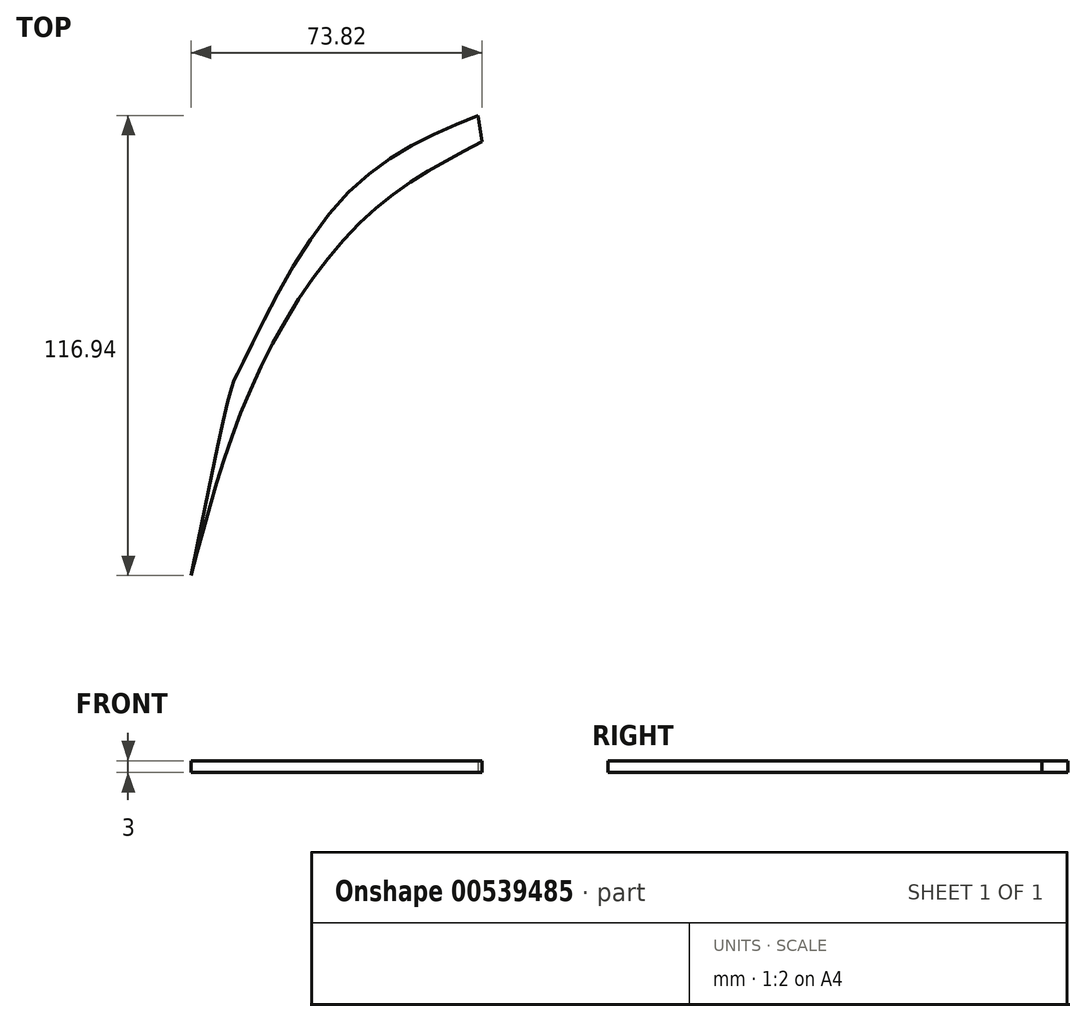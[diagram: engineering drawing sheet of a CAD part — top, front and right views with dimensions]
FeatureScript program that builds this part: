
annotation { "Feature Type Name" : "Feature", "Feature Type Description" : "" }
export const myFeature = defineFeature(function(context is Context, id is Id, definition is map)
    precondition{}
    {
        {
            var Q0;
            Q0=qCreatedBy(makeId("Top.planeOp"),FACE);
            var sketch = newSketch(context, id + "F0", { "sketchPlane" : qUnion([Q0])});
            skLineSegment(sketch, "E0.bottom", {"start": v(-86.95, -34.92) * mm, "end": v(12.45, -34.92) * mm});
            skLineSegment(sketch, "E0.top", {"start": v(-86.95, 85.08) * mm, "end": v(12.45, 85.08) * mm});
            skLineSegment(sketch, "E0.left", {"start": v(-86.95, -34.92) * mm, "end": v(-86.95, 85.08) * mm});
            skLineSegment(sketch, "E0.right", {"start": v(12.45, -34.92) * mm, "end": v(12.45, 85.08) * mm});
            skSolve(sketch);
        }
        {
            var Q0;
            Q0=makeQuery(id+"F0.imprint","IMPRINT",FACE,{"disambiguationData":[TD([[makeQuery(id+"F0.imprint","IMPRINT",EDGE,{"derivedFrom":sQuery(id+"F0.wireOp",EDGE,"E0.bottom")}),1.0]])]});
            var sketch = newSketch(context, id + "F1", { "sketchPlane" : qUnion([Q0])});
            skFitSpline(sketch, "E1", {"points": [v(-82.89, -33.95) * mm, v(-72.6, 14.09) * mm, v(-70.83, 17.96) * mm, v(-46.3, 59.8) * mm, v(-10.03, 82.99) * mm], "startDerivative": vector(41.06, 204.3) * mm, "endDerivative": vector(130.59, 53.62) * mm});
            skFitSpline(sketch, "E2", {"points": [v(-82.89, -33.95) * mm, v(-67.92, 13.16) * mm, v(-39.6, 56.22) * mm, v(-9.07, 76.32) * mm], "startDerivative": vector(34.97, 135.61) * mm, "endDerivative": vector(105.5, 54.96) * mm});
            skLineSegment(sketch, "E3", {"start": v(-10.03, 82.99) * mm, "end": v(-9.07, 76.32) * mm});
            skSolve(sketch);
        }
        {
            var Q0;
            Q0 = qSketchRegion(id + "F1", true);
            extrude(context, id + "F2", {"entities" : qUnion([Q0]), "depth" : 3 * mm, "offsetDistance" : 25 * mm});
        }
    });
